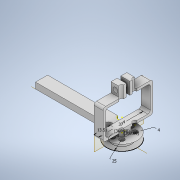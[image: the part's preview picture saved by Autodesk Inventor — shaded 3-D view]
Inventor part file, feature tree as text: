
AUTODESK INVENTOR PART (.ipt)
format: ipt  version: 2022 (Build 260153000, 153)  size: 257,536 bytes
history: native  units: mm
features: sketch x8, extrude x6, plane x1, fillet x1
ambient origin geometry x8: Origin, YZ Plane, XZ Plane, XY Plane, X Axis, Y Axis, Z Axis, Center Point
bodies: Solid1 (feature_tree)
feature tree (16):
  sketch  "Sketch1"  dims[d0=25.0mm d3=4.0mm]
  extrude  "Extrusion1"  Depth=25.0mm
  extrude  "Extrusion2"  Depth=4.0mm
  sketch  "Sketch4"  dims[d9=20.0mm d11=360.0deg d13=5.0mm d14=0.0mm]
  extrude  "Extrusion6"  Depth=5.0mm TaperAngle=0.0deg
  sketch  "Sketch30"  dims[d26=70.0mm d27=4.0mm d28=4.0mm]
  sketch  "Sketch31"  dims[d29=4.0mm d30=4.0mm]
  plane  "Work Plane4"
  extrude  "Extrusion14"  TaperAngle=90.0deg  [1 undecoded]
  extrude  "Extrusion15"  Depth=4.0mm
  fillet  "Fillet3"  Radius=4.0mm
  extrude  "Extrusion17"  Depth=4.0mm
  sketch  "Sketch2"  dims[d4=40.0mm d6=360.0deg d8=4.0mm]
  sketch  "Sketch8"  dims[d24=10.0mm d25=90.0deg]
  sketch  "Sketch41"  dims[d31=5.0mm d32=0.0mm]
  sketch  "Sketch42"  dims[d50=6.0mm d51=6.0mm d52=6.0mm d53=6.0mm d54=39.25mm d55=0.0mm d90=13.51mm d91=37.0mm d105=90.0deg d129=2.0mm d130=41.0mm d131=25.0mm d132=41.0mm d138=3.0mm d139=10.0mm d140=5.0mm d141=5.0mm d142=10.0mm d143=0.0mm d144=4.0mm d145=0.0mm d146=0.0mm d147=2.0mm d150=0.0mm d151=0.0mm d73=0.5mm d74=0.872665mm d75=0.5mm d76=0.872665mm d89=0.5mm d92=0.872665mm d152=0.5mm d153=0.872665mm]
note: 1 required parameter value undecoded (feature->parameter linkage not recoverable at this tier; creation-order binding heuristic only, values carry confidence <= 0.55)
